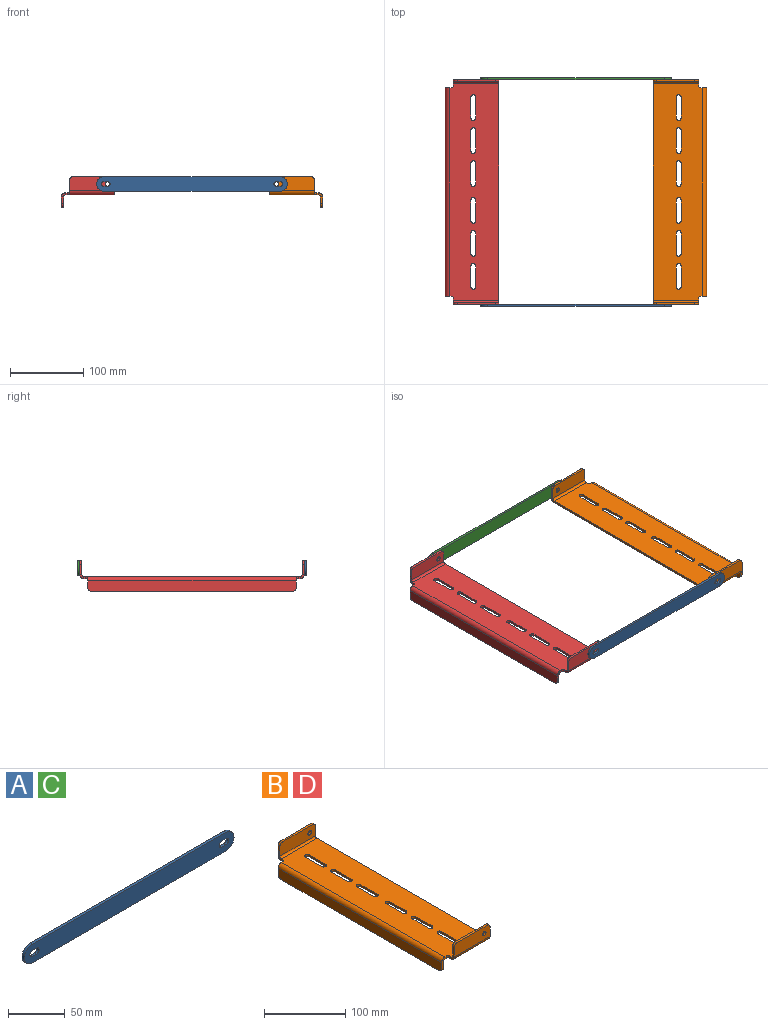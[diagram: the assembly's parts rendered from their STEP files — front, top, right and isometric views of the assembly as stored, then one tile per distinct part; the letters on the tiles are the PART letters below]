
ASSEMBLY  parts=4 mates=5
PART A: 14 faces, bbox 260x3x20 mm
  f0: plane 260x20mm, normal (0,-1,0), area 4982.8mm2, adj f2,f3,f4,f5,f6,f7,f8,f9
  f1: plane 260x20mm, normal (0,1,0), area 4982.8mm2, adj f2,f3,f4,f5,f6,f7,f8,f9
  f2: cylinder r=10mm len=20mm, axis (0,1,0), area 94.2mm2, adj f0,f1,f3,f5
  f3: plane 240x3mm, normal (0,0,-1), area 720mm2, adj f0,f1,f2,f4
  f4: cylinder r=10mm len=20mm, axis (0,1,0), area 94.2mm2, adj f0,f1,f3,f5
  f5: plane 240x3mm, normal (0,0,1), area 720mm2, adj f0,f1,f2,f4
  f6: plane 5x3mm, normal (0,0,1), area 15mm2, adj f0,f1,f7,f9
  f7: cylinder r=3.25mm len=6.5mm, axis (0,-1,0), area 30.6mm2, adj f0,f1,f6,f8
  f8: plane 5x3mm, normal (0,0,-1), area 15mm2, adj f0,f1,f7,f9
  f9: cylinder r=3.25mm len=6.5mm, axis (0,-1,0), area 30.6mm2, adj f0,f1,f6,f8
  f10: cylinder r=3.25mm len=6.5mm, axis (0,-1,0), area 30.6mm2, adj f0,f1,f11,f12
  f11: plane 5x3mm, normal (0,0,1), area 15mm2, adj f0,f1,f10,f13
  f12: plane 5x3mm, normal (0,0,-1), area 15mm2, adj f0,f1,f10,f13
  f13: cylinder r=3.25mm len=6.5mm, axis (0,-1,0), area 30.6mm2, adj f0,f1,f11,f12
PART B: 68 faces, bbox 73x306x42 mm
  f0: plane 28.5x3mm, normal (-1,0,0), area 85.5mm2, adj f1,f28,f29,f30
  f1: cylinder r=3.25mm len=6.5mm, axis (0,0,1), area 30.6mm2, adj f0,f2,f29,f30
  f2: plane 28.5x3mm, normal (1,0,0), area 85.5mm2, adj f1,f28,f29,f30
  f3: plane 28.5x3mm, normal (-1,0,0), area 85.5mm2, adj f4,f27,f29,f30
  f4: cylinder r=3.25mm len=6.5mm, axis (0,0,1), area 30.6mm2, adj f3,f5,f29,f30
  f5: plane 28.5x3mm, normal (1,0,0), area 85.5mm2, adj f4,f27,f29,f30
  f6: plane 28.5x3mm, normal (-1,0,0), area 85.5mm2, adj f7,f26,f29,f30
  f7: cylinder r=3.25mm len=6.5mm, axis (0,0,1), area 30.6mm2, adj f6,f8,f29,f30
  f8: plane 28.5x3mm, normal (1,0,0), area 85.5mm2, adj f7,f26,f29,f30
  f9: plane 3x2.3mm, normal (0,1,0), area 6.9mm2, adj f29,f30,f32,f65
  f10: plane 3x2.3mm, normal (-1,0,0), area 6.9mm2, adj f29,f30,f32,f53
  f11: plane 294.6x3mm, normal (1,0,0), area 883.8mm2, adj f29,f30,f42,f54
  f12: plane 3x2.3mm, normal (-1,0,0), area 6.9mm2, adj f29,f30,f31,f41
  f13: plane 3x2.3mm, normal (0,-1,0), area 6.9mm2, adj f29,f30,f31,f64
  f14: plane 28.5x3mm, normal (-1,0,0), area 85.5mm2, adj f15,f25,f29,f30
  f15: cylinder r=3.25mm len=6.5mm, axis (0,0,1), area 30.6mm2, adj f14,f16,f29,f30
  f16: plane 28.5x3mm, normal (1,0,0), area 85.5mm2, adj f15,f25,f29,f30
  f17: plane 28.5x3mm, normal (-1,0,0), area 85.5mm2, adj f18,f24,f29,f30
  f18: cylinder r=3.25mm len=6.5mm, axis (0,0,1), area 30.6mm2, adj f17,f19,f29,f30
  f19: plane 28.5x3mm, normal (1,0,0), area 85.5mm2, adj f18,f24,f29,f30
  f20: plane 28.5x3mm, normal (-1,0,0), area 85.5mm2, adj f21,f23,f29,f30
  f21: cylinder r=3.25mm len=6.5mm, axis (0,0,1), area 30.6mm2, adj f20,f22,f29,f30
  f22: plane 28.5x3mm, normal (1,0,0), area 85.5mm2, adj f21,f23,f29,f30
  f23: cylinder r=3.25mm len=6.5mm, axis (0,0,1), area 30.6mm2, adj f20,f22,f29,f30
  f24: cylinder r=3.25mm len=6.5mm, axis (0,0,1), area 30.6mm2, adj f17,f19,f29,f30
  f25: cylinder r=3.25mm len=6.5mm, axis (0,0,1), area 30.6mm2, adj f14,f16,f29,f30
  f26: cylinder r=3.25mm len=6.5mm, axis (0,0,1), area 30.6mm2, adj f6,f8,f29,f30
  f27: cylinder r=3.25mm len=6.5mm, axis (0,0,1), area 30.6mm2, adj f3,f5,f29,f30
  f28: cylinder r=3.25mm len=6.5mm, axis (0,0,1), area 30.6mm2, adj f0,f2,f29,f30
  f29: plane 294.6x67.3mm, normal (0,0,-1), area 18463.7mm2, adj f0,f1,f2,f3,f4,f5,f6,f7
  f30: plane 294.6x67.3mm, normal (0,0,1), area 18463.7mm2, adj f0,f1,f2,f3,f4,f5,f6,f7
  f31: cylinder r=3mm len=3mm, axis (0,0,-1), area 14.1mm2, adj f12,f13,f29,f30
  f32: cylinder r=3mm len=3mm, axis (0,0,-1), area 14.1mm2, adj f9,f10,f29,f30
  f33: plane 52x3mm, normal (0,0,1), area 156mm2, adj f37,f38,f39,f40
  f34: plane 14.3x3mm, normal (-1,0,0), area 42.9mm2, adj f37,f38,f40,f41
  f35: cylinder r=3.1mm len=6.2mm, axis (0,-1,0), area 58.4mm2, adj f37,f38
  f36: plane 14.3x3mm, normal (1,0,0), area 42.9mm2, adj f37,f38,f39,f42
  f37: plane 62x19.3mm, normal (0,-1,0), area 1155.7mm2, adj f33,f34,f35,f36,f39,f40,f43
  f38: plane 62x19.3mm, normal (0,1,0), area 1155.7mm2, adj f33,f34,f35,f36,f39,f40,f44
  f39: cylinder r=5mm len=5mm, axis (0,-1,0), area 23.6mm2, adj f33,f36,f37,f38
  f40: cylinder r=5mm len=5mm, axis (0,-1,0), area 23.6mm2, adj f33,f34,f37,f38
  f41: plane 5.7x5.7mm, normal (-1,0,0), area 19.8mm2, adj f12,f34,f43,f44
  f42: plane 5.7x5.7mm, normal (1,0,0), area 19.8mm2, adj f11,f36,f43,f44
  f43: cylinder r=5.7mm len=62mm, axis (-1,0,0), area 555.1mm2, adj f29,f37,f41,f42
  f44: cylinder r=2.7mm len=62mm, axis (-1,0,0), area 263mm2, adj f30,f38,f41,f42
  f45: plane 52x3mm, normal (0,0,1), area 156mm2, adj f49,f50,f51,f52
  f46: plane 14.3x3mm, normal (1,0,0), area 42.9mm2, adj f49,f50,f52,f54
  f47: cylinder r=3.1mm len=6.2mm, axis (0,1,0), area 58.4mm2, adj f49,f50
  f48: plane 14.3x3mm, normal (-1,0,0), area 42.9mm2, adj f49,f50,f51,f53
  f49: plane 62x19.3mm, normal (0,1,0), area 1155.7mm2, adj f45,f46,f47,f48,f51,f52,f55
  f50: plane 62x19.3mm, normal (0,-1,0), area 1155.7mm2, adj f45,f46,f47,f48,f51,f52,f56
  f51: cylinder r=5mm len=5mm, axis (0,1,0), area 23.6mm2, adj f45,f48,f49,f50
  f52: cylinder r=5mm len=5mm, axis (0,1,0), area 23.6mm2, adj f45,f46,f49,f50
  f53: plane 5.7x5.7mm, normal (-1,0,0), area 19.8mm2, adj f10,f48,f55,f56
  f54: plane 5.7x5.7mm, normal (1,0,0), area 19.8mm2, adj f11,f46,f55,f56
  f55: cylinder r=5.7mm len=62mm, axis (-1,0,0), area 555.1mm2, adj f29,f49,f53,f54
  f56: cylinder r=2.7mm len=62mm, axis (-1,0,0), area 263mm2, adj f30,f50,f53,f54
  f57: plane 274x3mm, normal (0,0,-1), area 822mm2, adj f60,f61,f62,f63
  f58: plane 9.3x3mm, normal (0,1,0), area 27.9mm2, adj f60,f61,f62,f65
  f59: plane 9.3x3mm, normal (0,-1,0), area 27.9mm2, adj f60,f61,f63,f64
  f60: plane 284x14.3mm, normal (1,0,0), area 4050.5mm2, adj f57,f58,f59,f62,f63,f67
  f61: plane 284x14.3mm, normal (-1,0,0), area 4050.5mm2, adj f57,f58,f59,f62,f63,f66
  f62: cylinder r=5mm len=5mm, axis (1,0,0), area 23.6mm2, adj f57,f58,f60,f61
  f63: cylinder r=5mm len=5mm, axis (1,0,0), area 23.6mm2, adj f57,f59,f60,f61
  f64: plane 5.7x5.7mm, normal (0,-1,0), area 19.8mm2, adj f13,f59,f66,f67
  f65: plane 5.7x5.7mm, normal (0,1,0), area 19.8mm2, adj f9,f58,f66,f67
  f66: cylinder r=5.7mm len=284mm, axis (0,-1,0), area 2542.8mm2, adj f30,f61,f64,f65
  f67: cylinder r=2.7mm len=284mm, axis (0,-1,0), area 1204.5mm2, adj f29,f60,f64,f65
PART C: same geometry as A
PART D: same geometry as B
PLACE A at identity fixed
PLACE B rot(axis=(0,0,-1),180deg) t=(0,0,0)mm
PLACE C t=(0,309,0)mm
PLACE D at identity fixed
MATE planar D.f30 <-> B.f30  axis (0,0,1) through (-105,0,3)mm
MATE parallel C.f5 <-> A.f5  axis (0,0,1) through (0,154.5,25)mm
MATE planar C.f0 <-> D.f49  axis (0,-1,0) through (0,153,15)mm
MATE cylindrical C.f4 <-> A.f4  axis (0,1,0) through (120,154.5,15)mm
MATE planar B.f49 <-> D.f37  axis (0,-1,0) through (136.55,-153,15.28)mm
